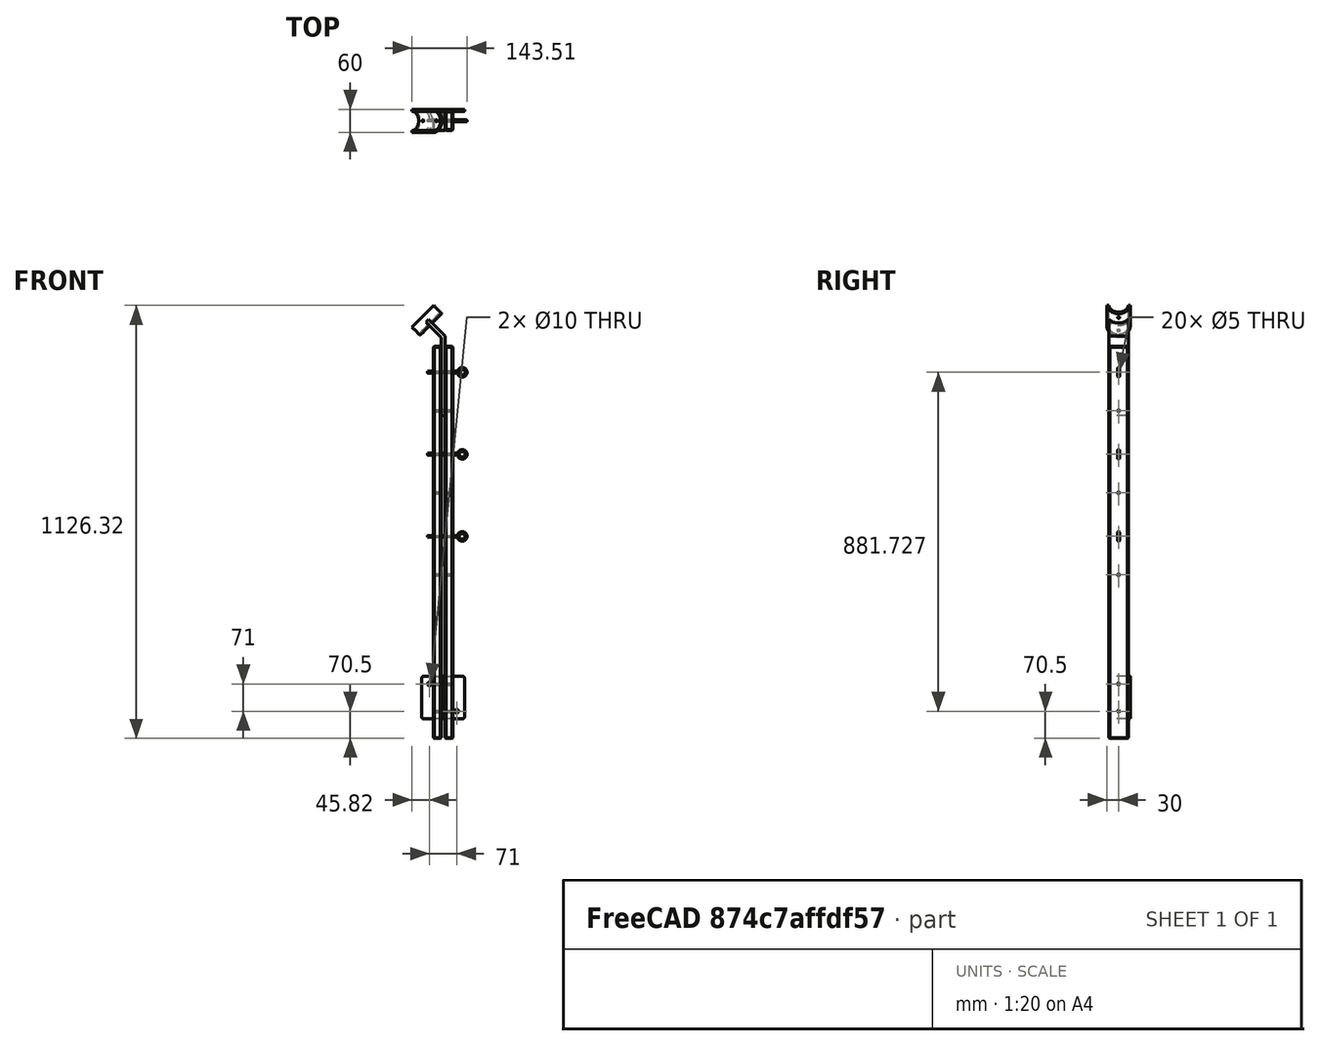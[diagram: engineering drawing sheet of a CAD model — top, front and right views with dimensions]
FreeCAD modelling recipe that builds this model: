
FCSTD DOCUMENT  (FreeCAD 0.17R10885 (Git))
Label: railing_first_element
License: All rights reserved
LicenseURL: http://en.wikipedia.org/wiki/All_rights_reserved
objects: Part::Part2DObjectPython×12, Part::FeaturePython×7, Part::Compound×4, Part::Cylinder×2, Part::Feature×1, App::Part×1, Part::Cut×1, Part::Mirroring×1
note: 28 computed .brp shape members not serialized (recipe doc carries the construction recipe); baked Part::Feature solids carry a one-line shape summary decoded from their .brp

FEATURE [Part::FeaturePython] railing_wood_01  # a2plus imported part (geometry in sourceFile) (typed FeaturePython)
  fixedPosition = true
  sourceFile = railing_wood.fcstd
  timeLastImport = 1.49253e+09
  updateColors = true
FEATURE [Part::Feature] Compound001_cs
  Placement = pos=(-77.8923,0,-170) rot=(0,0,1;0rad)
  shape: bbox 1490 x 3e-07 x 1728 mm, 0 faces, 0 solids (baked)
FEATURE [Part::Part2DObjectPython] Line  # Draft 2D object (typed FeaturePython)
  ChamferSize = 0
  Closed = false
  End = (-35.6937,-365,-86.0859)
  FilletRadius = 0
  Length = 220.312
  MakeFace = true
  Points = (2) [(-191.478,-365,69.6984),(-35.6937,-365,-86.0859)]
  Start = (-191.478,-365,69.6984)
  Subdivisions = 0
FEATURE [Part::Part2DObjectPython] Line001  # Draft 2D object (typed FeaturePython)
  ChamferSize = 0
  Closed = false
  End = (708.599,-365,658.207)
  FilletRadius = 0
  Length = 220.312
  MakeFace = true
  Points = (2) [(552.815,-365,813.991),(708.599,-365,658.207)]
  Start = (552.815,-365,813.991)
  Subdivisions = 0
FEATURE [Part::Part2DObjectPython] Line002  # Draft 2D object (typed FeaturePython)
  ChamferSize = 0
  Closed = false
  End = (630.707,-30,736.099)
  FilletRadius = 0
  Length = 1052.59
  MakeFace = true
  Points = (2) [(-113.586,-30,-8.19375),(630.707,-30,736.099)]
  Start = (-113.586,-30,-8.19375)
  Subdivisions = 0
FEATURE [Part::FeaturePython] test_01  label="handrail_holder"  # a2plus imported part (geometry in sourceFile) (typed FeaturePython)
  Placement = pos=(0,-3.2e-11,1000) rot=(0,0,1;0rad)
  fixedPosition = false
  sourceFile = handrail_holder.fcstd
  timeLastImport = 1.49254e+09
  updateColors = true
FEATURE [Part::FeaturePython] railing_plate_02  # a2plus imported part (geometry in sourceFile) (typed FeaturePython)
  Placement = pos=(4e-11,30,86) rot=(0,0,1;0rad)
  fixedPosition = false
  sourceFile = railing_plate.fcstd
  timeLastImport = 1.49258e+09
  updateColors = true
FEATURE [Part::Cylinder] Cylinder004
  Angle = 360
  AttacherType = Attacher::AttachEngine3D
  Height = 100
  Placement = pos=(-50,0,-35.5) rot=(0,1,0;1.5708rad)
  Radius = 2.5
FEATURE [Part::Part2DObjectPython] Line003  # Draft 2D object (typed FeaturePython)
  ChamferSize = 0
  Closed = false
  End = (-63.6396,-3.2e-11,1032.07)
  FilletRadius = 0
  Length = 1414.21
  MakeFace = true
  Placement = pos=(-1063.64,-3.2e-11,32.0711) rot=(0,0,1;0rad)
  Points = (2) [(0,0,0),(1000,0,1000)]
  Start = (-1063.64,-3.2e-11,32.0711)
  Subdivisions = 0
FEATURE [Part::Part2DObjectPython] Line004  # Draft 2D object (typed FeaturePython)
  ChamferSize = 0
  Closed = false
  End = (363.32,-3.2e-11,605.111)
  FilletRadius = 0
  Length = 1414.21
  MakeFace = true
  Placement = pos=(-636.68,-3.2e-11,-394.889) rot=(0,0,1;0rad)
  Points = (2) [(0,0,0),(1000,0,1000)]
  Start = (-636.68,-3.2e-11,-394.889)
  Subdivisions = 0
FEATURE [Part::Part2DObjectPython] Line005  # Draft 2D object (typed FeaturePython)
  ChamferSize = 0
  Closed = false
  End = (-743.419,-3.2e-11,-288.15)
  FilletRadius = 0
  Length = 150.952
  MakeFace = true
  Points = (2) [(-636.68,-3.20189e-11,-394.889),(-743.419,-3.20254e-11,-288.15)]
  Start = (-636.68,-3.2e-11,-394.889)
  Subdivisions = 0
FEATURE [Part::Part2DObjectPython] Line006  # Draft 2D object (typed FeaturePython)
  ChamferSize = 0
  Closed = false
  End = (256.581,-3.2e-11,711.85)
  FilletRadius = 0
  Length = 1414.21
  MakeFace = true
  Placement = pos=(-743.419,-3.2e-11,-288.15) rot=(0,0,1;0rad)
  Points = (2) [(0,0,0),(1000,0,1000)]
  Start = (-743.419,-3.2e-11,-288.15)
  Subdivisions = 0
FEATURE [Part::Part2DObjectPython] Line007  # Draft 2D object (typed FeaturePython)
  ChamferSize = 0
  Closed = false
  End = (149.842,-3.2e-11,818.589)
  FilletRadius = 0
  Length = 1414.21
  MakeFace = true
  Placement = pos=(-850.158,-3.2e-11,-181.411) rot=(0,0,1;0rad)
  Points = (2) [(0,0,0),(1000,0,1000)]
  Start = (-850.158,-3.2e-11,-181.411)
  Subdivisions = 0
FEATURE [Part::Part2DObjectPython] Line008  # Draft 2D object (typed FeaturePython)
  ChamferSize = 0
  Closed = false
  End = (-850.158,-3.2e-11,-181.411)
  FilletRadius = 0
  Length = 150.952
  MakeFace = true
  Placement = pos=(-106.739,0,106.739) rot=(0,0,1;0rad)
  Points = (2) [(-636.68,-3.20189e-11,-394.889),(-743.419,-3.20254e-11,-288.15)]
  Start = (-743.419,-3.2e-11,-288.15)
  Subdivisions = 0
FEATURE [Part::Part2DObjectPython] Line009  # Draft 2D object (typed FeaturePython)
  ChamferSize = 0
  Closed = false
  End = (-956.897,-3.2e-11,-74.6714)
  FilletRadius = 0
  Length = 150.952
  MakeFace = true
  Placement = pos=(-213.478,0,213.478) rot=(0,0,1;0rad)
  Points = (2) [(-636.68,-3.20189e-11,-394.889),(-743.419,-3.20254e-11,-288.15)]
  Start = (-850.158,-3.2e-11,-181.411)
  Subdivisions = 0
FEATURE [Part::Part2DObjectPython] Line010  # Draft 2D object (typed FeaturePython)
  ChamferSize = 0
  Closed = false
  End = (43.1028,-3.2e-11,925.329)
  FilletRadius = 0
  Length = 1414.21
  MakeFace = true
  Placement = pos=(-956.897,-3.2e-11,-74.6714) rot=(0,0,1;0rad)
  Points = (2) [(0,0,0),(1000,0,1000)]
  Start = (-956.897,-3.2e-11,-74.6714)
  Subdivisions = 0
FEATURE [Part::Part2DObjectPython] Line011  label="rope_vertical_offset"  # Draft 2D object (typed FeaturePython)
  ChamferSize = 0
  Closed = false
  End = (-50,0,191.79)
  FilletRadius = 0
  Length = 213.479
  MakeFace = true
  Points = (2) [(-50,-6.82854e-15,405.269),(-50,-6.82854e-15,191.79)]
  Start = (-50,0,405.269)
  Subdivisions = 0
FEATURE [App::Part] Part  label="drawing"
  Group = -> [Line,Line001,Line002,Compound001_cs,Line003,Line004,Line005,Line006,Line007,Line008,Line009,Line010,Line011]
  License = CC BY 3.0
  LicenseURL = http://creativecommons.org/licenses/by/3.0/
  Origin = -> PartOrigin
FEATURE [Part::Cylinder] Cylinder005  label="Cylinder"
  Angle = 360
  AttacherType = Attacher::AttachEngine3D
  Height = 100
  Placement = pos=(-50,0,405.269) rot=(0,1,0;1.5708rad)
  Radius = 2.5
  expr: Placement.Base.z = Compound003.Placement.Base.z
FEATURE [Part::FeaturePython] Array001  # Draft array (typed FeaturePython)
  Angle = 360
  ArrayType = 0
  Axis = (0,0,1)
  Base = -> Cylinder005
  Center = (0,0,0)
  Fuse = false
  IntervalAxis = (0,0,0)
  IntervalX = (0,0,100)
  IntervalY = (0,0,0)
  IntervalZ = (0,0,213.479)
  NumberPolar = 1
  NumberX = 2
  NumberY = 1
  NumberZ = 3
  expr: IntervalZ.z = rope_vertical_offset.Length
FEATURE [Part::FeaturePython] Component  label="Cylinder005"  # WARN: FeaturePython — macro-defined, semantics opaque (R4)
  CloneOf = -> Cylinder004
  HorizontalArea = 0
  MoveWithHost = false
  PerimeterLength = 0
  Placement = pos=(-50,0,35.5) rot=(0,1,0;1.5708rad)
  Role = 0
  VerticalArea = 0
FEATURE [Part::Compound] Compound004
  Links = -> [Cylinder004,Component]
  Placement = pos=(0,0,86) rot=(0,0,1;0rad)
  expr: Placement.Base.z = railing_plate_02.Placement.Base.z
FEATURE [Part::Compound] Compound001
  Links = -> [Array001,Compound004]
FEATURE [Part::Cut] Cut
  Base = -> railing_wood_01
  Tool = -> Compound001
FEATURE [Part::FeaturePython] eyelet_002  # a2plus imported part (geometry in sourceFile) (typed FeaturePython)
  Placement = pos=(-49.689,0,100) rot=(0,0,1;0rad)
  fixedPosition = false
  sourceFile = eyelet.fcstd
  timeLastImport = 1.49253e+09
  updateColors = true
FEATURE [Part::Mirroring] mirror  label="Mirror of eyelet_01"
  Base = (0,1,0)
  Normal = (1,0,0)
  Source = -> eyelet_002
FEATURE [Part::Compound] Compound003
  Links = -> [mirror]
  Placement = pos=(0,0,405.269) rot=(0,0,1;0rad)
FEATURE [Part::FeaturePython] Array  # Draft array (typed FeaturePython)
  Angle = 360
  ArrayType = 0
  Axis = (0,0,1)
  Base = -> Compound003
  Center = (0,0,0)
  Fuse = false
  IntervalAxis = (0,0,0)
  IntervalX = (0,0,213.479)
  IntervalY = (0,0,0)
  IntervalZ = (0,0,0)
  NumberPolar = 1
  NumberX = 3
  NumberY = 1
  NumberZ = 1
  expr: IntervalX.z = rope_vertical_offset.Length
FEATURE [Part::Compound] Compound  label="Railing_element"
  Links = -> [Cut,test_01,railing_plate_02,Array]
